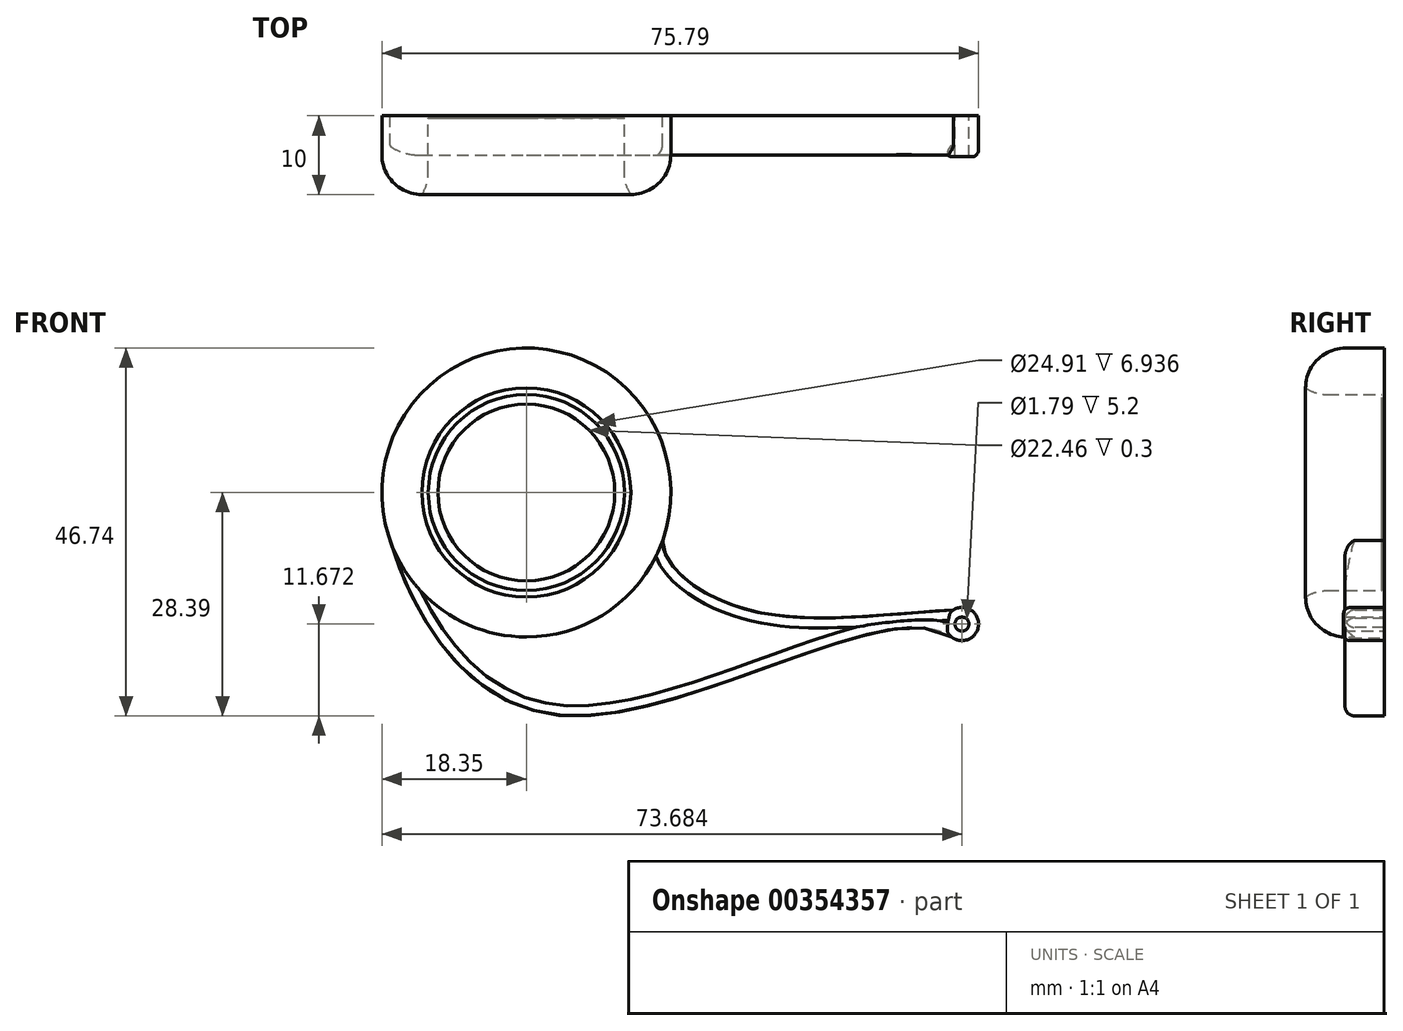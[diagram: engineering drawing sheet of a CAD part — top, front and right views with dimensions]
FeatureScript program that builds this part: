
annotation { "Feature Type Name" : "Feature", "Feature Type Description" : "" }
export const myFeature = defineFeature(function(context is Context, id is Id, definition is map)
    precondition{}
    {
        {
            var Q0;
            Q0=qCreatedBy(makeId("Front.planeOp"),FACE);
            var sketch = newSketch(context, id + "F0", { "sketchPlane" : qUnion([Q0])});
            skCircle(sketch, "E0", {"center": v(0, 0) * mm, "radius": 12.45 * mm});
            skCircle(sketch, "E1", {"center": v(0, 0) * mm, "radius": 18.35 * mm});
            skCircle(sketch, "E2", {"center": v(0, 0) * mm, "radius": 3.81 * mm});
            skFitSpline(sketch, "E3", {"points": [v(-17.3, -6.1) * mm, v(4.72, -28.34) * mm, v(54.2, -18.49) * mm], "startDerivative": vector(19.76, -63.27) * mm, "endDerivative": vector(42.47, -33.06) * mm});
            skFitSpline(sketch, "E4", {"points": [v(17.3, -6.1) * mm, v(27.03, -14.58) * mm, v(54.25, -14.92) * mm], "startDerivative": vector(0, -24.56) * mm, "endDerivative": vector(52.25, 3.3) * mm});
            skPoint(sketch, "E5", {"position": v(55.33, -16.72) * mm});
            skCircle(sketch, "E6", {"center": v(55.33, -16.72) * mm, "radius": 2.1 * mm});
            skCircle(sketch, "E7", {"center": v(55.33, -16.72) * mm, "radius": 0.9 * mm});
            skCircle(sketch, "E8", {"center": v(0, 0) * mm, "radius": 11.23 * mm});
            skSolve(sketch);
        }
        {
            var Q0;
            Q0=makeQuery(id+"F0.imprint","IMPRINT",FACE,{"disambiguationData":[TD([[makeQuery(id+"F0.imprint","IMPRINT",EDGE,{"derivedFrom":sQuery(id+"F0.wireOp",EDGE,"E0")}),-1.0]])]});
            extrude(context, id + "F1", {"entities" : qUnion([Q0]), "depth" : 10 * mm});
        }
        {
            var Q0;
            {var subQ3=sQuery(id+"F0.wireOp",EDGE,"E4");Q0=makeQuery(id+"F0.imprint","IMPRINT",FACE,{"disambiguationData":[TD([[makeQuery(id+"F0.imprint","IMPRINT",EDGE,{"derivedFrom":subQ3}),-1.0]])]});}
            extrude(context, id + "F2", {"entities" : qUnion([Q0]), "operationType" : NewBodyOperationType.ADD, "depth" : 5 * mm});
        }
        {
            var Q0;
            Q0=makeQuery(id+"F1.opExtrude","CAP_EDGE",EDGE,{"disambiguationData":[OSD([sQuery(id+"F0.wireOp",EDGE,"E1")])],"isStart":false});
            fillet(context, id + "F3", {"entities" : qUnion([Q0]), "radius" : 5.08 * mm, "tangentPropagation" : true, "allowEdgeOverflow" : false});
        }
        {
            var Q0;
            Q0=makeQuery(id+"F1.opExtrude","CAP_EDGE",EDGE,{"disambiguationData":[OSD([sQuery(id+"F0.wireOp",EDGE,"E0")])],"isStart":false});
            fillet(context, id + "F4", {"entities" : qUnion([Q0]), "radius" : 5.08 * mm, "tangentPropagation" : true, "allowEdgeOverflow" : false});
        }
        {
            var Q0;
            Q0=makeQuery(id+"F2.opExtrude","CAP_EDGE",EDGE,{"disambiguationData":[OSD([sQuery(id+"F0.wireOp",EDGE,"E3")])],"isStart":false});
            var Q1;
            Q1=makeQuery(id+"F2.opExtrude","CAP_EDGE",EDGE,{"disambiguationData":[OSD([sQuery(id+"F0.wireOp",EDGE,"E4")])],"isStart":false});
            fillet(context, id + "F5", {"entities" : qUnion([Q0, Q1]), "radius" : 1.27 * mm, "tangentPropagation" : true, "allowEdgeOverflow" : false});
        }
        {
            var Q0;
            Q0=makeQuery(id+"F0.imprint","IMPRINT",FACE,{"disambiguationData":[TD([[makeQuery(id+"F0.imprint","IMPRINT",EDGE,{"derivedFrom":sQuery(id+"F0.wireOp",EDGE,"E7")}),-1.0]])]});
            extrude(context, id + "F6", {"entities" : qUnion([Q0]), "operationType" : NewBodyOperationType.ADD, "depth" : 5.2 * mm});
        }
        {
            var Q0;
            Q0=makeQuery(id+"F6.opExtrude","CAP_EDGE",EDGE,{"disambiguationData":[OSD([sQuery(id+"F0.wireOp",EDGE,"E6")])],"isStart":false});
            fillet(context, id + "F7", {"entities" : qUnion([Q0]), "radius" : 0.86 * mm, "tangentPropagation" : true, "allowEdgeOverflow" : false});
        }
        {
            var Q0;
            Q0=makeQuery(id+"F0.imprint","IMPRINT",FACE,{"disambiguationData":[TD([[makeQuery(id+"F0.imprint","IMPRINT",EDGE,{"derivedFrom":sQuery(id+"F0.wireOp",EDGE,"E0")}),1.0]])]});
            extrude(context, id + "F8", {"entities" : qUnion([Q0]), "operationType" : NewBodyOperationType.ADD, "depth" : 0.3 * mm});
        }
    });
